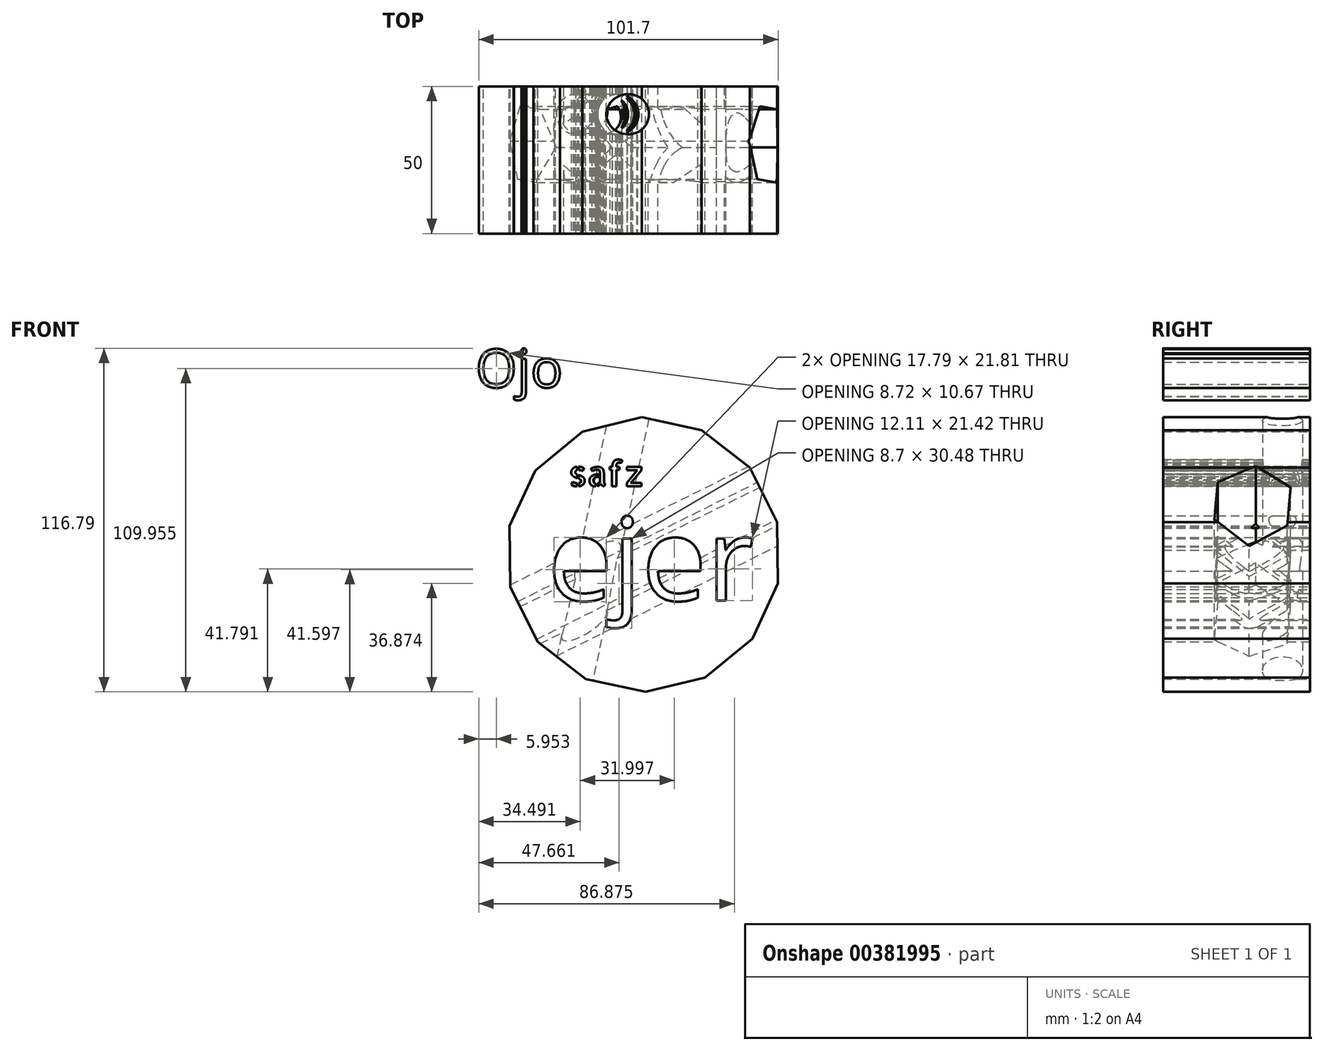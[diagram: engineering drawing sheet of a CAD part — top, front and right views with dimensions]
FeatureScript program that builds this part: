
annotation { "Feature Type Name" : "Feature", "Feature Type Description" : "" }
export const myFeature = defineFeature(function(context is Context, id is Id, definition is map)
    precondition{}
    {
        {
            var Q0;
            Q0=qCreatedBy(makeId("Front.planeOp"),FACE);
            var sketch = newSketch(context, id + "F0", { "sketchPlane" : qUnion([Q0])});
            skCircle(sketch, "E0.cCircle", {"center": v(0, 0) * mm, "radius": 45.51 * mm, "construction": true});
            skLineSegment(sketch, "E0.0", {"start": v(-36.89, 28.62) * mm, "end": v(-20.82, 41.79) * mm});
            skLineSegment(sketch, "E0.1", {"start": v(-20.82, 41.79) * mm, "end": v(-0.62, 46.68) * mm});
            skLineSegment(sketch, "E0.2", {"start": v(-0.62, 46.68) * mm, "end": v(19.7, 42.33) * mm});
            skLineSegment(sketch, "E0.3", {"start": v(19.7, 42.33) * mm, "end": v(36.1, 29.6) * mm});
            skLineSegment(sketch, "E0.4", {"start": v(36.1, 29.6) * mm, "end": v(45.37, 11) * mm});
            skLineSegment(sketch, "E0.5", {"start": v(45.37, 11) * mm, "end": v(45.65, -9.78) * mm});
            skLineSegment(sketch, "E0.6", {"start": v(45.65, -9.78) * mm, "end": v(36.89, -28.62) * mm});
            skLineSegment(sketch, "E0.7", {"start": v(36.89, -28.62) * mm, "end": v(20.82, -41.79) * mm});
            skLineSegment(sketch, "E0.8", {"start": v(20.82, -41.79) * mm, "end": v(0.62, -46.68) * mm});
            skLineSegment(sketch, "E0.9", {"start": v(0.62, -46.68) * mm, "end": v(-19.7, -42.33) * mm});
            skLineSegment(sketch, "E0.10", {"start": v(-19.7, -42.33) * mm, "end": v(-36.1, -29.6) * mm});
            skLineSegment(sketch, "E0.11", {"start": v(-36.1, -29.6) * mm, "end": v(-45.37, -11) * mm});
            skLineSegment(sketch, "E0.12", {"start": v(-45.37, -11) * mm, "end": v(-45.65, 9.78) * mm});
            skLineSegment(sketch, "E0.13", {"start": v(-45.65, 9.78) * mm, "end": v(-36.89, 28.62) * mm});
            skPoint(sketch, "E0.0.midPoint", {"position": v(-28.85, 35.2) * mm});
            skText(sketch, "E1", { "text": "Ojo", "fontName": "OpenSans-Regular.ttf"});
            const initialGuessF0  = {"E1": [-0.05716, 0.0568, 1, 0, 0.01306]};
            skSetInitialGuess(sketch, initialGuessF0);
            skSolve(sketch);
        }
        {
            var Q0;
            Q0 = qSketchRegion(id + "F0", true);
            extrude(context, id + "F1", {"entities" : qUnion([Q0]), "depth" : 50 * mm});
        }
        {
            var Q0;
            Q0=qCreatedBy(makeId("Front.planeOp"),FACE);
            var sketch = newSketch(context, id + "F2", { "sketchPlane" : qUnion([Q0])});
            skText(sketch, "E2", { "text": "ejer", "fontName": "OpenSans-Regular.ttf"});
            const initialGuessF2  = {"E2": [-0.03266, -0.0156, 1, 0, 0.0283]};
            skSetInitialGuess(sketch, initialGuessF2);
            skSolve(sketch);
        }
        {
            var Q0;
            Q0=makeQuery(id+"F1.opExtrude","CAP_FACE",FACE,{"disambiguationData":[OSD([sQuery(id+"F0.wireOp",EDGE,"E0.0"),sQuery(id+"F0.wireOp",EDGE,"E0.1"),sQuery(id+"F0.wireOp",EDGE,"E0.2"),sQuery(id+"F0.wireOp",EDGE,"E0.3"),sQuery(id+"F0.wireOp",EDGE,"E0.4"),sQuery(id+"F0.wireOp",EDGE,"E0.5"),sQuery(id+"F0.wireOp",EDGE,"E0.6"),sQuery(id+"F0.wireOp",EDGE,"E0.7"),sQuery(id+"F0.wireOp",EDGE,"E0.8"),sQuery(id+"F0.wireOp",EDGE,"E0.9"),sQuery(id+"F0.wireOp",EDGE,"E0.10"),sQuery(id+"F0.wireOp",EDGE,"E0.11"),sQuery(id+"F0.wireOp",EDGE,"E0.12"),sQuery(id+"F0.wireOp",EDGE,"E0.13")])],"isStart":false});
            var Q1;
            Q1 = qSketchRegion(id + "F2", true);
            var Q2;
            Q2=makeQuery(id+"F2.imprint","IMPRINT",FACE,{"disambiguationData":[TD([[makeQuery(id+"F2.imprint","IMPRINT",EDGE,{"derivedFrom":sQuery(id+"F2.wireOp",EDGE,"E2.sketch_text.stroke-50")}),1.0]])]});
            var Q3;
            Q3=makeQuery(id+"F2.imprint","IMPRINT",FACE,{"disambiguationData":[TD([[makeQuery(id+"F2.imprint","IMPRINT",EDGE,{"derivedFrom":sQuery(id+"F2.wireOp",EDGE,"E2.sketch_text.stroke-36")}),-1.0]])]});
            var Q4;
            Q4=makeQuery(id+"F2.imprint","IMPRINT",FACE,{"disambiguationData":[TD([[makeQuery(id+"F2.imprint","IMPRINT",EDGE,{"derivedFrom":sQuery(id+"F2.wireOp",EDGE,"E2.sketch_text.stroke-14")}),1.0]])]});
            var Q5;
            Q5=makeQuery(id+"F2.imprint","IMPRINT",FACE,{"disambiguationData":[TD([[makeQuery(id+"F2.imprint","IMPRINT",EDGE,{"derivedFrom":sQuery(id+"F2.wireOp",EDGE,"E2.sketch_text.stroke-0")}),-1.0]])]});
            var Q6;
            Q6=makeQuery(id+"F2.imprint","IMPRINT",FACE,{"disambiguationData":[TD([[makeQuery(id+"F2.imprint","IMPRINT",EDGE,{"derivedFrom":sQuery(id+"F2.wireOp",EDGE,"E2.sketch_text.stroke-55")}),-1.0]])]});
            var Q7;
            Q7=makeQuery(id+"F2.imprint","IMPRINT",FACE,{"disambiguationData":[TD([[makeQuery(id+"F2.imprint","IMPRINT",EDGE,{"derivedFrom":sQuery(id+"F2.wireOp",EDGE,"E2.sketch_text.stroke-28")}),-1.0]])]});
            extrude(context, id + "F3", {"entities" : qUnion([Q0, Q1, Q2, Q3, Q4, Q5, Q6, Q7]), "operationType" : NewBodyOperationType.REMOVE, "endBound" : BoundingType.THROUGH_ALL, "depth" : 25 * mm});
        }
        {
            var Q0;
            Q0=makeQuery(id+"F1.opExtrude","SWEPT_FACE",FACE,{"disambiguationData":[OSD([sQuery(id+"F0.wireOp",EDGE,"E0.9")])]});
            var sketch = newSketch(context, id + "F4", { "sketchPlane" : qUnion([Q0])});
            skCircle(sketch, "E3", {"center": v(-14.78, 9.42) * mm, "radius": 6.82 * mm});
            skSolve(sketch);
        }
        {
            var Q0;
            Q0 = qSketchRegion(id + "F4", true);
            extrude(context, id + "F5", {"entities" : qUnion([Q0]), "operationType" : NewBodyOperationType.REMOVE, "endBound" : BoundingType.THROUGH_ALL, "oppositeDirection" : true, "depth" : 25 * mm});
        }
        {
            var Q0;
            Q0=makeQuery(id+"F1.opExtrude","CAP_FACE",FACE,{"disambiguationData":[OSD([sQuery(id+"F0.wireOp",EDGE,"E0.0"),sQuery(id+"F0.wireOp",EDGE,"E0.1"),sQuery(id+"F0.wireOp",EDGE,"E0.2"),sQuery(id+"F0.wireOp",EDGE,"E0.3"),sQuery(id+"F0.wireOp",EDGE,"E0.4"),sQuery(id+"F0.wireOp",EDGE,"E0.5"),sQuery(id+"F0.wireOp",EDGE,"E0.6"),sQuery(id+"F0.wireOp",EDGE,"E0.7"),sQuery(id+"F0.wireOp",EDGE,"E0.8"),sQuery(id+"F0.wireOp",EDGE,"E0.9"),sQuery(id+"F0.wireOp",EDGE,"E0.10"),sQuery(id+"F0.wireOp",EDGE,"E0.11"),sQuery(id+"F0.wireOp",EDGE,"E0.12"),sQuery(id+"F0.wireOp",EDGE,"E0.13")])],"isStart":false});
            var sketch = newSketch(context, id + "F6", { "sketchPlane" : qUnion([Q0])});
            skText(sketch, "E4", { "text": "safz", "fontName": "AllertaStencil-Regular.ttf"});
            const initialGuessF6  = {"E4": [-0.02547, 0.02324, 1, 0, 0.00857]};
            skSetInitialGuess(sketch, initialGuessF6);
            skSolve(sketch);
        }
        {
            var Q0;
            Q0 = qSketchRegion(id + "F6", true);
            extrude(context, id + "F7", {"entities" : qUnion([Q0]), "operationType" : NewBodyOperationType.REMOVE, "endBound" : BoundingType.THROUGH_ALL, "oppositeDirection" : true, "depth" : 25 * mm});
        }
        {
            var Q0;
            Q0=makeQuery(id+"F1.opExtrude","SWEPT_FACE",FACE,{"disambiguationData":[OSD([sQuery(id+"F0.wireOp",EDGE,"E0.4")])]});
            var sketch = newSketch(context, id + "F8", { "sketchPlane" : qUnion([Q0])});
            skCircle(sketch, "E5.cCircle", {"center": v(-19.63, -3.3) * mm, "radius": 12.44 * mm, "construction": true});
            skPoint(sketch, "E5.cCircle.perimeterSnap0", {"position": v(-25, 10.39) * mm});
            skLineSegment(sketch, "E5.0", {"start": v(-31.47, 4.8) * mm, "end": v(-18.53, 11) * mm});
            skLineSegment(sketch, "E5.1", {"start": v(-18.53, 11) * mm, "end": v(-6.68, 2.9) * mm});
            skLineSegment(sketch, "E5.2", {"start": v(-6.68, 2.9) * mm, "end": v(-7.78, -11.42) * mm});
            skLineSegment(sketch, "E5.3", {"start": v(-7.78, -11.42) * mm, "end": v(-20.73, -17.63) * mm});
            skLineSegment(sketch, "E5.4", {"start": v(-20.73, -17.63) * mm, "end": v(-32.58, -9.51) * mm});
            skLineSegment(sketch, "E5.5", {"start": v(-32.58, -9.51) * mm, "end": v(-31.47, 4.8) * mm});
            skPoint(sketch, "E5.0.midPoint", {"position": v(-25, 7.9) * mm});
            skPoint(sketch, "E5.0.midPoint.positionSnap0", {"position": v(-25, 10.39) * mm});
            skSolve(sketch);
        }
        {
            var Q0;
            Q0 = qSketchRegion(id + "F8", true);
            extrude(context, id + "F9", {"entities" : qUnion([Q0]), "operationType" : NewBodyOperationType.REMOVE, "endBound" : BoundingType.THROUGH_ALL, "oppositeDirection" : true, "depth" : 25 * mm});
        }
    });
